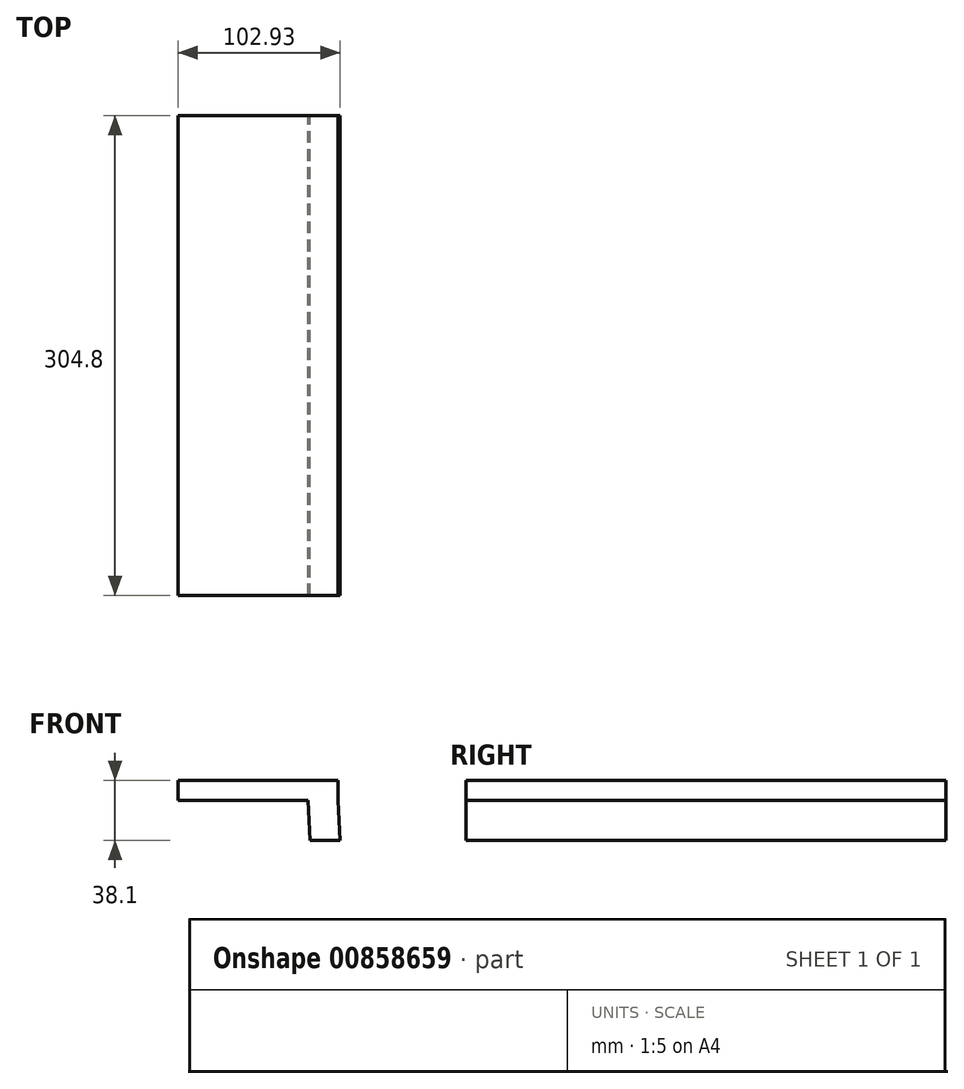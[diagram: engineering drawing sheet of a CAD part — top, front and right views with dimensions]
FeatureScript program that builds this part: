
annotation { "Feature Type Name" : "Feature", "Feature Type Description" : "" }
export const myFeature = defineFeature(function(context is Context, id is Id, definition is map)
    precondition{}
    {
        {
            var Q0;
            Q0=qCreatedBy(makeId("Front.planeOp"),FACE);
            var sketch = newSketch(context, id + "F0", { "sketchPlane" : qUnion([Q0])});
            skLineSegment(sketch, "E0.bottom", {"start": v(50.8, -6.35) * mm, "end": v(-50.8, -6.35) * mm});
            skLineSegment(sketch, "E0.top", {"start": v(50.8, 6.35) * mm, "end": v(-50.8, 6.35) * mm});
            skLineSegment(sketch, "E0.left", {"start": v(50.8, -6.35) * mm, "end": v(50.8, 6.35) * mm});
            skLineSegment(sketch, "E0.right", {"start": v(-50.8, -6.35) * mm, "end": v(-50.8, 6.35) * mm});
            skPoint(sketch, "E0.middle", {"position": v(0, 0) * mm});
            skLineSegment(sketch, "E1", {"start": v(-50.8, -6.35) * mm, "end": v(-50.8, -31.75) * mm, "construction": true});
            skLineSegment(sketch, "E2", {"start": v(-50.8, -31.75) * mm, "end": v(101.6, -31.75) * mm, "construction": true});
            skLineSegment(sketch, "E3", {"start": v(50.8, -6.35) * mm, "end": v(52.13, -31.75) * mm});
            skLineSegment(sketch, "E4", {"start": v(31.75, -6.35) * mm, "end": v(33.08, -31.75) * mm});
            skLineSegment(sketch, "E5", {"start": v(33.08, -31.75) * mm, "end": v(52.13, -31.75) * mm});
            skLineSegment(sketch, "E6", {"start": v(31.75, -6.35) * mm, "end": v(50.8, -6.35) * mm});
            skPoint(sketch, "E7", {"position": v(41.23, 6.35) * mm});
            skSolve(sketch);
        }
        {
            var Q0;
            Q0=makeQuery(id+"F0.imprint","IMPRINT",FACE,{"disambiguationData":[TD([[makeQuery(id+"F0.imprint","IMPRINT",EDGE,{"derivedFrom":sQuery(id+"F0.wireOp",EDGE,"E0.bottom")}),-1.0]])]});
            extrude(context, id + "F1", {"entities" : qUnion([Q0]), "depth" : 304.8 * mm, "offsetDistance" : 25.4 * mm});
        }
        {
            var Q0;
            Q0=makeQuery(id+"F0.imprint","IMPRINT",FACE,{"disambiguationData":[TD([[makeQuery(id+"F0.imprint","IMPRINT",EDGE,{"derivedFrom":sQuery(id+"F0.wireOp",EDGE,"E3")}),-1.0]])]});
            extrude(context, id + "F2", {"entities" : qUnion([Q0]), "operationType" : NewBodyOperationType.ADD, "depth" : 304.8 * mm, "offsetDistance" : 25.4 * mm});
        }
    });
